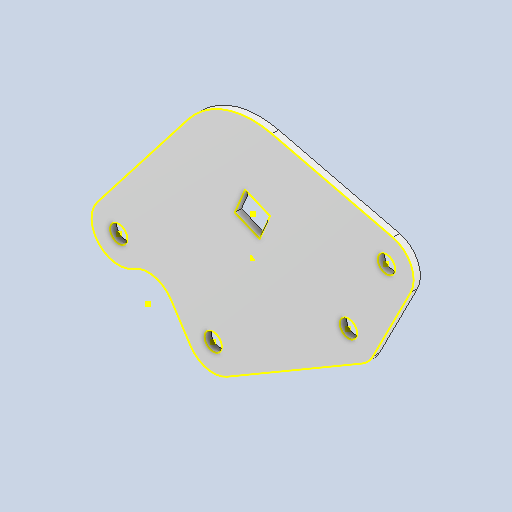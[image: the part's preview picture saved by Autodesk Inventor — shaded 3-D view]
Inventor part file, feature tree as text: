
AUTODESK INVENTOR PART (.ipt)
format: ipt  version: 2025.2 (Build 292293000, 293)  size: 250,880 bytes
history: native  units: in
note: dims shown in document units (in); Inventor stores cm internally (conversion verified against a paired STEP export)
features: other x5, sketch x2, plane x1, sheet_metal_op x1, reference x1
ambient origin geometry x8: Origin, YZ Plane, XZ Plane, XY Plane, X Axis, Y Axis, Z Axis, Center Point
bodies: Body1 (feature_tree)
feature tree (10):
  plane  "Work Plane1"
  sheet_metal_op  "Face3"
  sketch  "Sketch2"  dims[d14=0.16in d15=0.0625in]
  sketch  "Sketch1"  dims[d1=0.5in]
  reference  "Reference3"
  other  "Plate3"
  parser-record x1  (decoder bookkeeping rows leaked as tree rows — omitted from the tree; the rows remain in map.json)
  other  "ACE 2.0.iam"
  other  "V5 Rotation Sensor:4"
  other  "Rear Vertical Odom Pod Rot Side:2"
note: 1 file-system path scrubbed to <path> (originals preserved in map.json)
